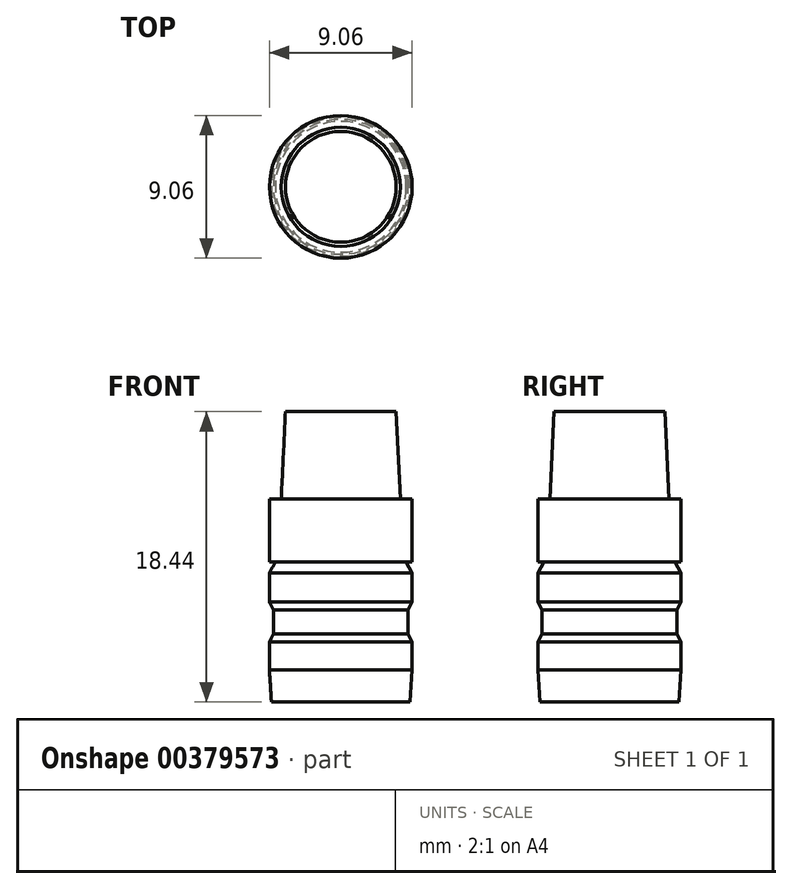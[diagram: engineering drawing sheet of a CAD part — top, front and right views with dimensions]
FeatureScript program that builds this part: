
annotation { "Feature Type Name" : "Feature", "Feature Type Description" : "" }
export const myFeature = defineFeature(function(context is Context, id is Id, definition is map)
    precondition{}
    {
        {
            var Q0;
            Q0=qCreatedBy(makeId("Front.planeOp"),FACE);
            var sketch = newSketch(context, id + "F0", { "sketchPlane" : qUnion([Q0])});
            skLineSegment(sketch, "E0", {"start": v(0, 0) * mm, "end": v(0, 18.44) * mm});
            skLineSegment(sketch, "E1", {"start": v(0, 18.44) * mm, "end": v(3.52, 18.44) * mm});
            skLineSegment(sketch, "E2", {"start": v(3.52, 18.44) * mm, "end": v(3.78, 12.88) * mm});
            skLineSegment(sketch, "E3", {"start": v(3.78, 12.88) * mm, "end": v(4.53, 12.88) * mm});
            skLineSegment(sketch, "E4", {"start": v(4.53, 12.88) * mm, "end": v(4.53, 8.9) * mm});
            skLineSegment(sketch, "E5", {"start": v(4.4, 0) * mm, "end": v(0, 0) * mm});
            skLineSegment(sketch, "E6.trimOffspring", {"start": v(4.53, 8.2) * mm, "end": v(4.53, 6.35) * mm});
            skLineSegment(sketch, "E7", {"start": v(4.53, 3.81) * mm, "end": v(4.28, 4.32) * mm});
            skLineSegment(sketch, "E8", {"start": v(4.28, 4.32) * mm, "end": v(4.28, 5.84) * mm});
            skLineSegment(sketch, "E9", {"start": v(4.28, 5.84) * mm, "end": v(4.53, 6.35) * mm});
            skLineSegment(sketch, "E10", {"start": v(4.4, 0) * mm, "end": v(4.53, 2.03) * mm});
            skPoint(sketch, "E11.orphan", {"position": v(4.53, 0) * mm});
            skLineSegment(sketch, "E12.trimOffspring", {"start": v(4.53, 3.81) * mm, "end": v(4.53, 2.03) * mm});
            skLineSegment(sketch, "E13", {"start": v(4.53, 8.2) * mm, "end": v(4.15, 8.9) * mm});
            skLineSegment(sketch, "E14", {"start": v(4.15, 8.9) * mm, "end": v(4.53, 8.9) * mm});
            skPoint(sketch, "E15.start.orphan", {"position": v(4.15, 8.2) * mm});
            skSolve(sketch);
        }
        {
            var Q0;
            Q0=makeQuery(id+"F0.imprint","IMPRINT",FACE,{"disambiguationData":[TD([[makeQuery(id+"F0.imprint","IMPRINT",EDGE,{"derivedFrom":sQuery(id+"F0.wireOp",EDGE,"E0")}),-1.0]])]});
            var Q1;
            Q1=sQuery(id+"F0.wireOp",EDGE,"E0");
            revolve(context, id + "F1", {"entities" : qUnion([Q0]), "axis" : qUnion([Q1]), "revolveType" : RevolveType.FULL});
        }
    });
